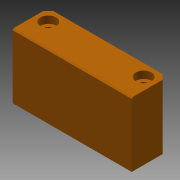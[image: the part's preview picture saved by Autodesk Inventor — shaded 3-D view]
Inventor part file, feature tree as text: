
AUTODESK INVENTOR PART (.ipt)
format: ipt  version: 2015 (Build 190159000, 159)  size: 103,936 bytes
history: native  units: mm
features: extrude x2, hole x2, chamfer x2, sketch x2
ambient origin geometry x8: Origin, YZ Plane, XZ Plane, XY Plane, X Axis, Y Axis, Z Axis, Center Point
bodies: Volumenkörper1 (feature_tree)
feature tree (8):
  extrude  "Extrusion1"  Depth=50.0mm
  hole  "Bohrung1"  [1 undecoded]
  hole  "Bohrung2"  [1 undecoded]
  chamfer  "Fase1"  Distance=10.0mm
  extrude  "Extrusion2"  Depth=12.0mm
  chamfer  "Fase2"  Distance=25.5mm
  sketch  "Skizze1"  dims[d0=15.0mm d1=50.0mm]
  sketch  "Skizze2"  dims[d2=27.0mm d3=0.0mm d4=5.0mm d5=5.0mm d6=3.4mm d7=6.0mm d8=6.5mm d9=3.0mm d10=90.0deg d11=8.0mm d12=20.594885mm d13=5.0mm d14=5.0mm d15=3.4mm d16=6.0mm d17=6.5mm d18=3.0mm d19=90.0deg d20=8.0mm d21=20.594885mm d22=0.5mm d23=2.0mm d24=45.0deg d25=10.0mm d26=10.0mm d27=12.0mm d28=25.5mm d29=0.0mm d30=2.0mm d31=2.0mm d32=45.0deg]
note: 2 required parameter values undecoded (feature->parameter linkage not recoverable at this tier; creation-order binding heuristic only, values carry confidence <= 0.55)
